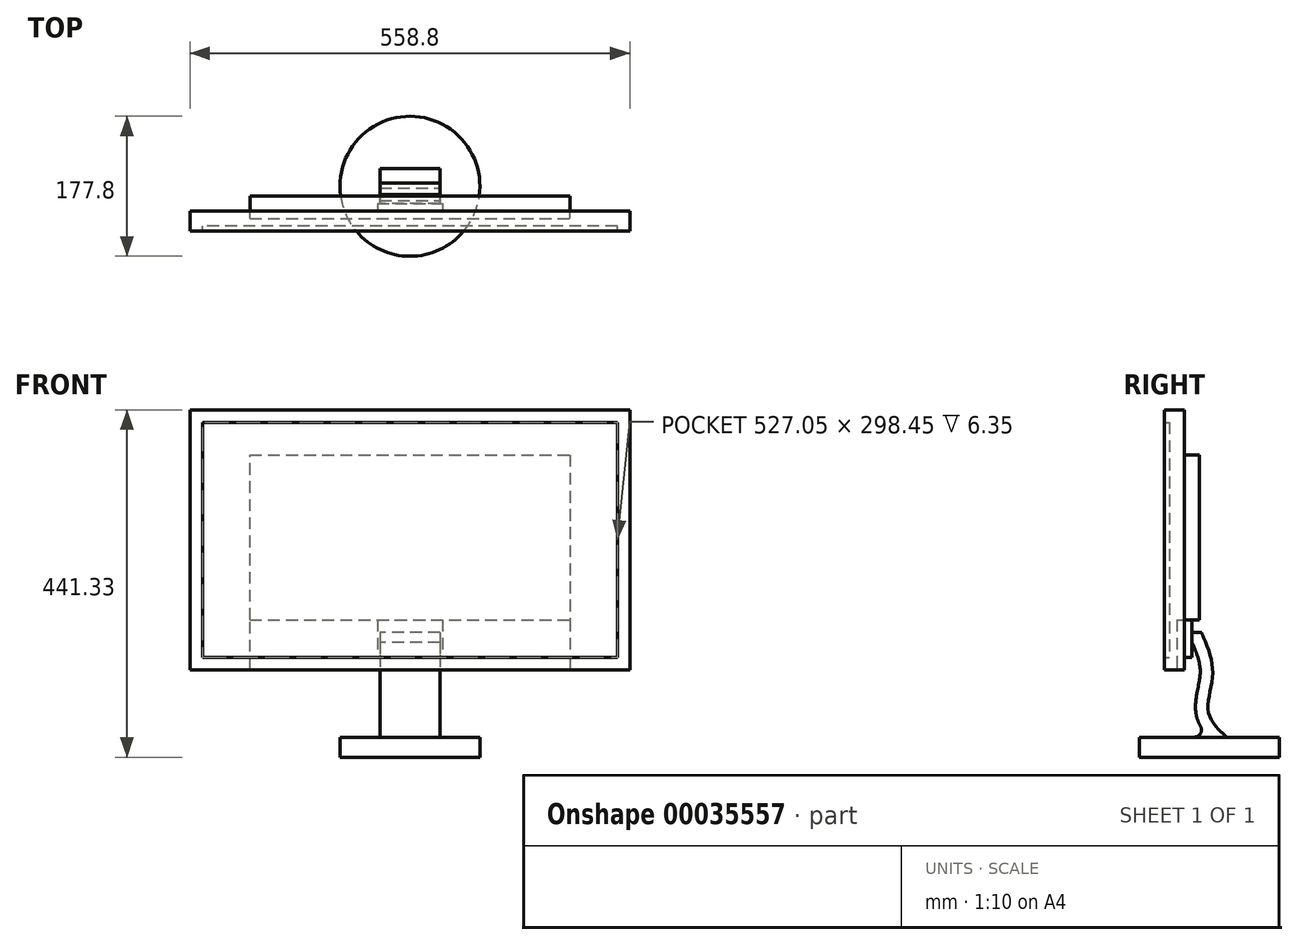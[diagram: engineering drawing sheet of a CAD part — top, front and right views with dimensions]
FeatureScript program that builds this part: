
annotation { "Feature Type Name" : "Feature", "Feature Type Description" : "" }
export const myFeature = defineFeature(function(context is Context, id is Id, definition is map)
    precondition{}
    {
        {
            var Q0;
            Q0=qCreatedBy(makeId("Front.planeOp"),FACE);
            var sketch = newSketch(context, id + "F0", { "sketchPlane" : qUnion([Q0])});
            skLineSegment(sketch, "E0.bottom", {"start": v(-289.1, 187.95) * mm, "end": v(269.7, 187.95) * mm});
            skLineSegment(sketch, "E0.top", {"start": v(-289.1, -142.25) * mm, "end": v(269.7, -142.25) * mm});
            skLineSegment(sketch, "E0.left", {"start": v(-289.1, 187.95) * mm, "end": v(-289.1, -142.25) * mm});
            skLineSegment(sketch, "E0.right", {"start": v(269.7, 187.95) * mm, "end": v(269.7, -142.25) * mm});
            skLineSegment(sketch, "E1", {"start": v(-273.23, 172.07) * mm, "end": v(-273.23, -126.38) * mm});
            skLineSegment(sketch, "E2", {"start": v(-273.23, -126.38) * mm, "end": v(253.82, -126.38) * mm});
            skLineSegment(sketch, "E3", {"start": v(253.82, -126.38) * mm, "end": v(253.82, 172.07) * mm});
            skLineSegment(sketch, "E4", {"start": v(253.82, 172.07) * mm, "end": v(-273.23, 172.07) * mm});
            skSolve(sketch);
        }
        {
            var Q0;
            Q0=makeQuery(id+"F0.imprint","IMPRINT",FACE,{"disambiguationData":[TD([[makeQuery(id+"F0.imprint","IMPRINT",EDGE,{"derivedFrom":sQuery(id+"F0.wireOp",EDGE,"E0.bottom")}),-1.0]])]});
            extrude(context, id + "F1", {"entities" : qUnion([Q0]), "depth" : 25.4 * mm});
        }
        {
            var Q0;
            Q0=makeQuery(id+"F0.imprint","IMPRINT",FACE,{"disambiguationData":[TD([[makeQuery(id+"F0.imprint","IMPRINT",EDGE,{"derivedFrom":sQuery(id+"F0.wireOp",EDGE,"E1")}),1.0]])]});
            extrude(context, id + "F2", {"entities" : qUnion([Q0]), "operationType" : NewBodyOperationType.ADD, "depth" : 19.05 * mm});
        }
        {
            var Q0;
            Q0=makeQuery(id+"F0.imprint","IMPRINT",FACE,{"disambiguationData":[TD([[makeQuery(id+"F0.imprint","IMPRINT",EDGE,{"derivedFrom":sQuery(id+"F0.wireOp",EDGE,"E1")}),1.0]])]});
            var sketch = newSketch(context, id + "F3", { "sketchPlane" : qUnion([Q0])});
            skLineSegment(sketch, "E5", {"start": v(-212.9, 130.8) * mm, "end": v(193.5, 130.8) * mm});
            skLineSegment(sketch, "E6", {"start": v(193.5, 130.8) * mm, "end": v(193.5, -78.75) * mm});
            skLineSegment(sketch, "E7", {"start": v(193.5, -78.75) * mm, "end": v(-212.9, -78.75) * mm});
            skLineSegment(sketch, "E8", {"start": v(-212.9, -78.75) * mm, "end": v(-212.9, 130.8) * mm});
            skSolve(sketch);
        }
        {
            var Q0;
            Q0=makeQuery(id+"F3.imprint","IMPRINT",FACE,{"disambiguationData":[TD([[makeQuery(id+"F3.imprint","IMPRINT",EDGE,{"derivedFrom":sQuery(id+"F3.wireOp",EDGE,"E5")}),-1.0]])]});
            extrude(context, id + "F4", {"entities" : qUnion([Q0]), "operationType" : NewBodyOperationType.ADD, "oppositeDirection" : true, "depth" : 19.05 * mm});
        }
        {
            var Q0;
            Q0=makeQuery(id+"F0.imprint","IMPRINT",FACE,{"disambiguationData":[TD([[makeQuery(id+"F0.imprint","IMPRINT",EDGE,{"derivedFrom":sQuery(id+"F0.wireOp",EDGE,"E1")}),1.0]])]});
            var sketch = newSketch(context, id + "F5", { "sketchPlane" : qUnion([Q0])});
            skPoint(sketch, "E9.0", {"position": v(193.5, -78.75) * mm});
            skPoint(sketch, "E10.0", {"position": v(-212.9, -78.75) * mm});
            skLineSegment(sketch, "E11", {"start": v(193.5, -78.75) * mm, "end": v(193.5, -142.25) * mm});
            skLineSegment(sketch, "E12", {"start": v(193.5, -142.25) * mm, "end": v(-212.9, -142.25) * mm});
            skLineSegment(sketch, "E13", {"start": v(-212.9, -142.25) * mm, "end": v(-212.9, -78.75) * mm});
            skLineSegment(sketch, "E14", {"start": v(-212.9, -78.75) * mm, "end": v(193.5, -78.75) * mm});
            skSolve(sketch);
        }
        {
            var Q0;
            {var subQ5=sQuery(id+"F5.wireOp",EDGE,"E12");Q0=makeQuery(id+"F5.imprint","IMPRINT",FACE,{"disambiguationData":[TD([[makeQuery(id+"F5.imprint","IMPRINT",EDGE,{"derivedFrom":subQ5}),-1.0]])]});}
            var Q1;
            {var subQ5=sQuery(id+"F5.wireOp",EDGE,"E14");Q1=makeQuery(id+"F5.imprint","IMPRINT",FACE,{"disambiguationData":[TD([[makeQuery(id+"F5.imprint","IMPRINT",EDGE,{"derivedFrom":subQ5}),-1.0]])]});}
            extrude(context, id + "F6", {"entities" : qUnion([Q0, Q1]), "operationType" : NewBodyOperationType.REMOVE, "depth" : 9.52 * mm});
        }
        {
            var Q0;
            {var subQ5=sQuery(id+"F5.wireOp",EDGE,"E14");Q0=makeQuery(id+"F5.imprint","IMPRINT",FACE,{"disambiguationData":[TD([[makeQuery(id+"F5.imprint","IMPRINT",EDGE,{"derivedFrom":subQ5}),-1.0]])]});}
            var sketch = newSketch(context, id + "F7", { "sketchPlane" : qUnion([Q0])});
            skLineSegment(sketch, "E15", {"start": v(31.57, -126.38) * mm, "end": v(-50.98, -126.38) * mm});
            skPoint(sketch, "E16.0", {"position": v(-212.9, -78.75) * mm});
            skLineSegment(sketch, "E17", {"start": v(-50.98, -78.75) * mm, "end": v(31.57, -78.75) * mm});
            skLineSegment(sketch, "E18", {"start": v(-50.98, -78.75) * mm, "end": v(-50.98, -126.38) * mm});
            skLineSegment(sketch, "E19", {"start": v(32, -78.67) * mm, "end": v(31.57, -126.38) * mm});
            skSolve(sketch);
        }
        {
            var Q0;
            {var subQ5=sQuery(id+"F7.wireOp",EDGE,"E15");Q0=makeQuery(id+"F7.imprint","IMPRINT",FACE,{"disambiguationData":[TD([[makeQuery(id+"F7.imprint","IMPRINT",EDGE,{"derivedFrom":subQ5}),1.0]])]});}
            extrude(context, id + "F8", {"entities" : qUnion([Q0]), "operationType" : NewBodyOperationType.ADD, "oppositeDirection" : true, "depth" : 9.52 * mm});
        }
        {
            var Q0;
            Q0=makeQuery(id+"F8.opExtrude","CAP_FACE",FACE,{"disambiguationData":[OSD([sQuery(id+"F5.wireOp",EDGE,"E14"),sQuery(id+"F7.wireOp",EDGE,"E15"),sQuery(id+"F7.wireOp",EDGE,"E17"),sQuery(id+"F7.wireOp",EDGE,"E18"),sQuery(id+"F7.wireOp",EDGE,"E19")])],"isStart":false});
            var sketch = newSketch(context, id + "F9", { "sketchPlane" : qUnion([Q0])});
            skLineSegment(sketch, "E20", {"start": v(-28.68, -94.63) * mm, "end": v(47.8, -94.63) * mm});
            skLineSegment(sketch, "E21", {"start": v(47.8, -94.63) * mm, "end": v(47.8, -126.38) * mm});
            skLineSegment(sketch, "E22", {"start": v(47.8, -126.38) * mm, "end": v(-28.68, -126.38) * mm});
            skLineSegment(sketch, "E23", {"start": v(-28.68, -94.63) * mm, "end": v(-28.68, -126.38) * mm});
            skSolve(sketch);
        }
        {
            var Q0;
            Q0=makeQuery(id+"F9.imprint","IMPRINT",FACE,{"disambiguationData":[TD([[makeQuery(id+"F9.imprint","IMPRINT",EDGE,{"derivedFrom":sQuery(id+"F9.wireOp",EDGE,"E20")}),-1.0]])]});
            extrude(context, id + "F10", {"entities" : qUnion([Q0]), "operationType" : NewBodyOperationType.ADD, "depth" : 44.45 * mm});
        }
        {
            var Q0;
            Q0=makeQuery(id+"F10.boolean.opBoolean","MERGE",FACE,{"derivedFrom":[makeQuery(id+"F8.opExtrude","SWEPT_FACE",FACE,{"disambiguationData":[OSD([sQuery(id+"F7.wireOp",EDGE,"E15")])]}),makeQuery(id+"F10.opExtrude","SWEPT_FACE",FACE,{"disambiguationData":[OSD([sQuery(id+"F9.wireOp",EDGE,"E22")])]})]});
            var sketch = newSketch(context, id + "F11", { "sketchPlane" : qUnion([Q0])});
            skLineSegment(sketch, "E24", {"start": v(28.68, -9.53) * mm, "end": v(-47.8, -9.53) * mm});
            skLineSegment(sketch, "E25", {"start": v(-47.8, -9.52) * mm, "end": v(-47.8, -53.98) * mm});
            skLineSegment(sketch, "E26", {"start": v(-47.8, -53.98) * mm, "end": v(28.68, -53.98) * mm});
            skLineSegment(sketch, "E27", {"start": v(28.68, -53.98) * mm, "end": v(28.68, -9.52) * mm});
            skSolve(sketch);
        }
        {
            var Q0;
            Q0=makeQuery(id+"F11.imprint","IMPRINT",FACE,{"disambiguationData":[TD([[makeQuery(id+"F11.imprint","IMPRINT",EDGE,{"derivedFrom":sQuery(id+"F11.wireOp",EDGE,"E24")}),1.0]])]});
            extrude(context, id + "F12", {"entities" : qUnion([Q0]), "operationType" : NewBodyOperationType.ADD, "depth" : 101.6 * mm});
        }
        {
            var Q0;
            Q0=makeQuery(id+"F12.opExtrude","CAP_FACE",FACE,{"disambiguationData":[OSD([sQuery(id+"F11.wireOp",EDGE,"E24"),sQuery(id+"F11.wireOp",EDGE,"E25"),sQuery(id+"F11.wireOp",EDGE,"E26"),sQuery(id+"F11.wireOp",EDGE,"E27")])],"isStart":false});
            var sketch = newSketch(context, id + "F13", { "sketchPlane" : qUnion([Q0])});
            skCircle(sketch, "E28", {"center": v(-9.56, -31.75) * mm, "radius": 88.9 * mm});
            skPoint(sketch, "E28.centerSnap0", {"position": v(-9.56, -53.98) * mm});
            skPoint(sketch, "E28.centerSnap1", {"position": v(28.68, -31.75) * mm});
            skSolve(sketch);
        }
        {
            var Q0;
            Q0=qSketchRegion(id+"F13",true);
            extrude(context, id + "F14", {"entities" : qUnion([Q0]), "operationType" : NewBodyOperationType.ADD, "depth" : 25.4 * mm});
        }
        {
            var Q0;
            Q0=makeQuery(id+"F12.boolean.opBoolean","MERGE",FACE,{"derivedFrom":[makeQuery(id+"F10.opExtrude","SWEPT_FACE",FACE,{"disambiguationData":[OSD([sQuery(id+"F9.wireOp",EDGE,"E21")])]}),makeQuery(id+"F12.opExtrude","SWEPT_FACE",FACE,{"disambiguationData":[OSD([sQuery(id+"F11.wireOp",EDGE,"E25")])]})]});
            var sketch = newSketch(context, id + "F15", { "sketchPlane" : qUnion([Q0])});
            skFitSpline(sketch, "E29", {"points": [v(-21.2, -94.63) * mm, v(-35.71, -146.34) * mm, v(-30.35, -196.38) * mm, v(-53.98, -227.98) * mm], "startDerivative": vector(-63.14, -143.08) * mm, "endDerivative": vector(-104.86, -93.64) * mm});
            skFitSpline(sketch, "E30.0", {"points": [v(-6.68, -101.04) * mm, v(-8, -104.02) * mm, v(-10.57, -109.85) * mm, v(-14.01, -118.26) * mm, v(-16.36, -124.97) * mm, v(-17.83, -130.15) * mm, v(-18.7, -133.95) * mm, v(-19.35, -137.66) * mm, v(-19.68, -140.68) * mm, v(-19.82, -143.06) * mm, v(-19.86, -144.54) * mm, v(-19.85, -145.72) * mm, v(-19.82, -146.9) * mm, v(-19.74, -148.44) * mm, v(-19.58, -150.36) * mm, v(-19.27, -153.02) * mm, v(-18.75, -156.52) * mm, v(-17.95, -160.96) * mm, v(-17.04, -165.6) * mm, v(-16.1, -170.43) * mm, v(-15.19, -175.44) * mm, v(-14.43, -180.62) * mm, v(-13.93, -186.02) * mm, v(-13.84, -190.72) * mm, v(-14.07, -194.6) * mm, v(-14.36, -197.09) * mm, v(-14.66, -198.85) * mm, v(-14.85, -199.86) * mm, v(-15.17, -201.36) * mm, v(-15.74, -203.57) * mm, v(-16.67, -206.4) * mm, v(-17.75, -209.12) * mm, v(-18.97, -211.7) * mm, v(-20.74, -215) * mm, v(-23.2, -218.84) * mm, v(-26.4, -223.02) * mm, v(-29.75, -226.85) * mm, v(-33.18, -230.4) * mm, v(-37.8, -234.82) * mm, v(-41.22, -237.87) * mm, v(-43.4, -239.82) * mm]});
            skLineSegment(sketch, "E31.0", {"start": v(-15.88, -126.38) * mm, "end": v(-15.88, -100.98) * mm});
            skLineSegment(sketch, "E31.1", {"start": v(-15.88, -221.63) * mm, "end": v(-15.88, -126.38) * mm});
            skLineSegment(sketch, "E31.2", {"start": v(-47.62, -221.63) * mm, "end": v(-15.87, -221.63) * mm});
            skLineSegment(sketch, "E31.3", {"start": v(-47.62, -100.98) * mm, "end": v(-47.62, -221.63) * mm});
            skLineSegment(sketch, "E31.4", {"start": v(-15.88, -100.98) * mm, "end": v(-47.62, -100.98) * mm});
            skSolve(sketch);
        }
        {
            var Q0;
            {var subQ3=sQuery(id+"F15.wireOp",EDGE,"E31.3");Q0=makeQuery(id+"F15.imprint","IMPRINT",FACE,{"disambiguationData":[TD([[makeQuery(id+"F15.imprint","IMPRINT",EDGE,{"derivedFrom":subQ3}),1.0]])]});}
            var Q1;
            {var subQ8=sQuery(id+"F15.wireOp",EDGE,"E31.3");Q1=makeQuery(id+"F15.imprint","IMPRINT",FACE,{"disambiguationData":[TD([[makeQuery(id+"F15.imprint","IMPRINT",EDGE,{"derivedFrom":subQ8}),-1.0]])]});}
            var Q2;
            {var subQ1=sQuery(id+"F15.wireOp",EDGE,"E30.0");var subQ3=sQuery(id+"F15.wireOp",EDGE,"E31.0");var subQ5=makeQuery(id+"F15.imprint","INTERSECT",VERTEX,{"derivedFrom":[subQ1,subQ3]});Q2=makeQuery(id+"F15.imprint","IMPRINT",FACE,{"disambiguationData":[TD([[makeQuery(id+"F15.imprint","IMPRINT",EDGE,{"disambiguationData":[TD([[subQ5,-1.0]])],"derivedFrom":subQ1}),1.0]])]});}
            var Q3;
            {var subQ0=sQuery(id+"F11.wireOp",EDGE,"E25");var subQ4=makeQuery(id+"F12.opExtrude","SWEPT_EDGE",EDGE,{"disambiguationData":[OSD([sQuery(id+"F7.wireOp",EDGE,"E15"),sQuery(id+"F11.wireOp",EDGE,"E24"),subQ0])]});Q3=makeQuery(id+"F15.imprint","IMPRINT",FACE,{"disambiguationData":[TD([[makeQuery(id+"F15.imprint","IMPRINT",EDGE,{"derivedFrom":subQ4}),1.0]])]});}
            var Q4;
            {var subQ1=sQuery(id+"F15.wireOp",EDGE,"E30.0");var subQ3=sQuery(id+"F15.wireOp",EDGE,"E31.1");var subQ5=makeQuery(id+"F15.imprint","INTERSECT",VERTEX,{"disambiguationData":[OD(1.0)],"derivedFrom":[subQ1,subQ3]});Q4=makeQuery(id+"F15.imprint","IMPRINT",FACE,{"disambiguationData":[TD([[makeQuery(id+"F15.imprint","IMPRINT",EDGE,{"disambiguationData":[TD([[subQ5,-1.0]])],"derivedFrom":subQ1}),1.0]])]});}
            extrude(context, id + "F16", {"entities" : qUnion([Q0, Q1, Q2, Q3, Q4]), "operationType" : NewBodyOperationType.REMOVE, "endBound" : BoundingType.UP_TO_NEXT, "oppositeDirection" : true, "depth" : 25.4 * mm});
        }
        {
            var Q0;
            Q0=makeQuery(id+"F16.boolean.opBoolean","COPY",EDGE,{"derivedFrom":makeQuery(id+"F16.opExtrude","SWEPT_EDGE",EDGE,{"disambiguationData":[OSD([sQuery(id+"F9.wireOp",EDGE,"E20"),sQuery(id+"F9.wireOp",EDGE,"E21"),sQuery(id+"F15.wireOp",EDGE,"E29")])]})});
            var Q1;
            {var subQ0=sQuery(id+"F11.wireOp",EDGE,"E26");Q1=makeQuery(id+"F16.boolean.opBoolean","MERGE",EDGE,{"derivedFrom":[makeQuery(id+"F12.opExtrude","CAP_EDGE",EDGE,{"disambiguationData":[OSD([subQ0])],"isStart":false}),makeQuery(id+"F16.opExtrude","SWEPT_EDGE",EDGE,{"disambiguationData":[OSD([subQ0,sQuery(id+"F11.wireOp",EDGE,"E27")])]})]});}
            var Q2;
            Q2=makeQuery(id+"F16.boolean.opBoolean","COPY",EDGE,{"derivedFrom":makeQuery(id+"F16.opExtrude","SWEPT_EDGE",EDGE,{"disambiguationData":[OSD([sQuery(id+"F11.wireOp",EDGE,"E25"),sQuery(id+"F15.wireOp",EDGE,"E30.0")])]})});
            var Q3;
            Q3=makeQuery(id+"F12.opExtrude","CAP_EDGE",EDGE,{"disambiguationData":[OSD([sQuery(id+"F11.wireOp",EDGE,"E25")])],"isStart":false});
            var Q4;
            Q4=makeQuery(id+"F12.opExtrude","CAP_EDGE",EDGE,{"disambiguationData":[OSD([sQuery(id+"F11.wireOp",EDGE,"E27")])],"isStart":false});
            fillet(context, id + "F17", {"entities" : qUnion([Q0, Q1, Q2, Q3, Q4]), "radius" : 9.34 * mm, "tangentPropagation" : true, "allowEdgeOverflow" : false});
        }
    });
